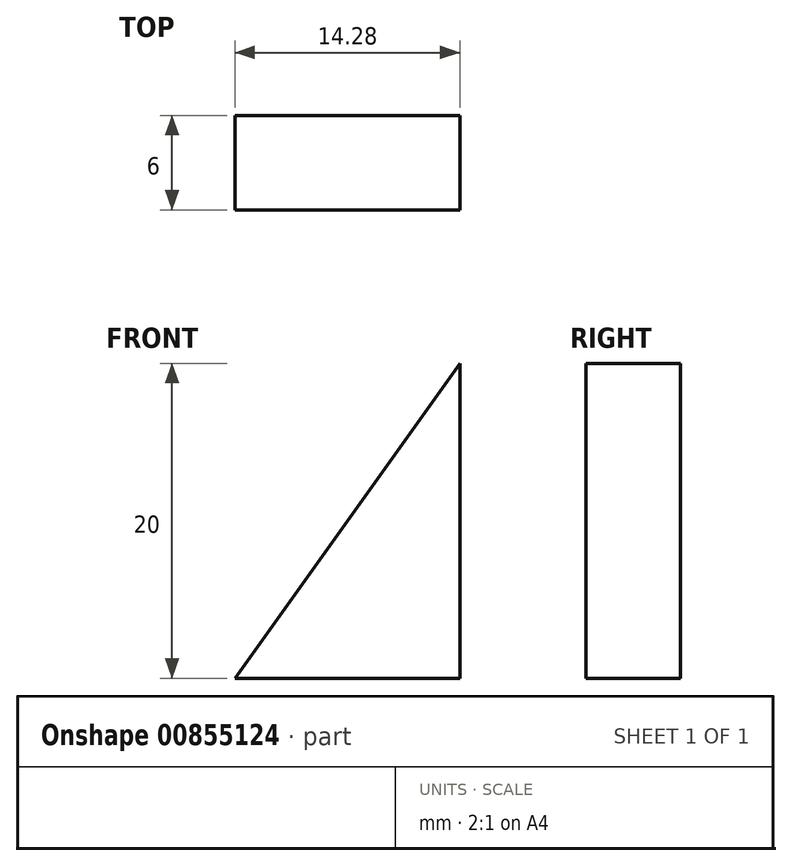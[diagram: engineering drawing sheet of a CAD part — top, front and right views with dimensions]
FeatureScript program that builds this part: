
annotation { "Feature Type Name" : "Feature", "Feature Type Description" : "" }
export const myFeature = defineFeature(function(context is Context, id is Id, definition is map)
    precondition{}
    {
        {
            var Q0;
            Q0=qCreatedBy(makeId("Top.planeOp"),FACE);
            var sketch = newSketch(context, id + "F0", { "sketchPlane" : qUnion([Q0])});
            skLineSegment(sketch, "E0.bottom", {"start": v(-7.14, 3) * mm, "end": v(7.14, 3) * mm});
            skLineSegment(sketch, "E0.top", {"start": v(-7.14, -3) * mm, "end": v(7.14, -3) * mm});
            skLineSegment(sketch, "E0.left", {"start": v(-7.14, 3) * mm, "end": v(-7.14, -3) * mm});
            skLineSegment(sketch, "E0.right", {"start": v(7.14, 3) * mm, "end": v(7.14, -3) * mm});
            skPoint(sketch, "E0.middle", {"position": v(0, 0) * mm});
            skSolve(sketch);
        }
        {
            var Q0;
            Q0=makeQuery(id+"F0.imprint","IMPRINT",FACE,{"disambiguationData":[TD([[makeQuery(id+"F0.imprint","IMPRINT",EDGE,{"derivedFrom":sQuery(id+"F0.wireOp",EDGE,"E0.bottom")}),-1.0]])]});
            extrude(context, id + "F1", {"entities" : qUnion([Q0]), "depth" : 20 * mm, "offsetDistance" : 25 * mm});
        }
        {
            var Q0;
            Q0=makeQuery(id+"F1.opExtrude","CAP_EDGE",EDGE,{"disambiguationData":[OSD([sQuery(id+"F0.wireOp",EDGE,"E0.left")])],"isStart":false});
            chamfer(context, id + "F2", {"entities" : qUnion([Q0]), "chamferType" : ChamferType.TWO_OFFSETS, "width1" : 14.28 * mm, "oppositeDirection" : false, "width2" : 20 * mm, "tangentPropagation" : true});
        }
    });
